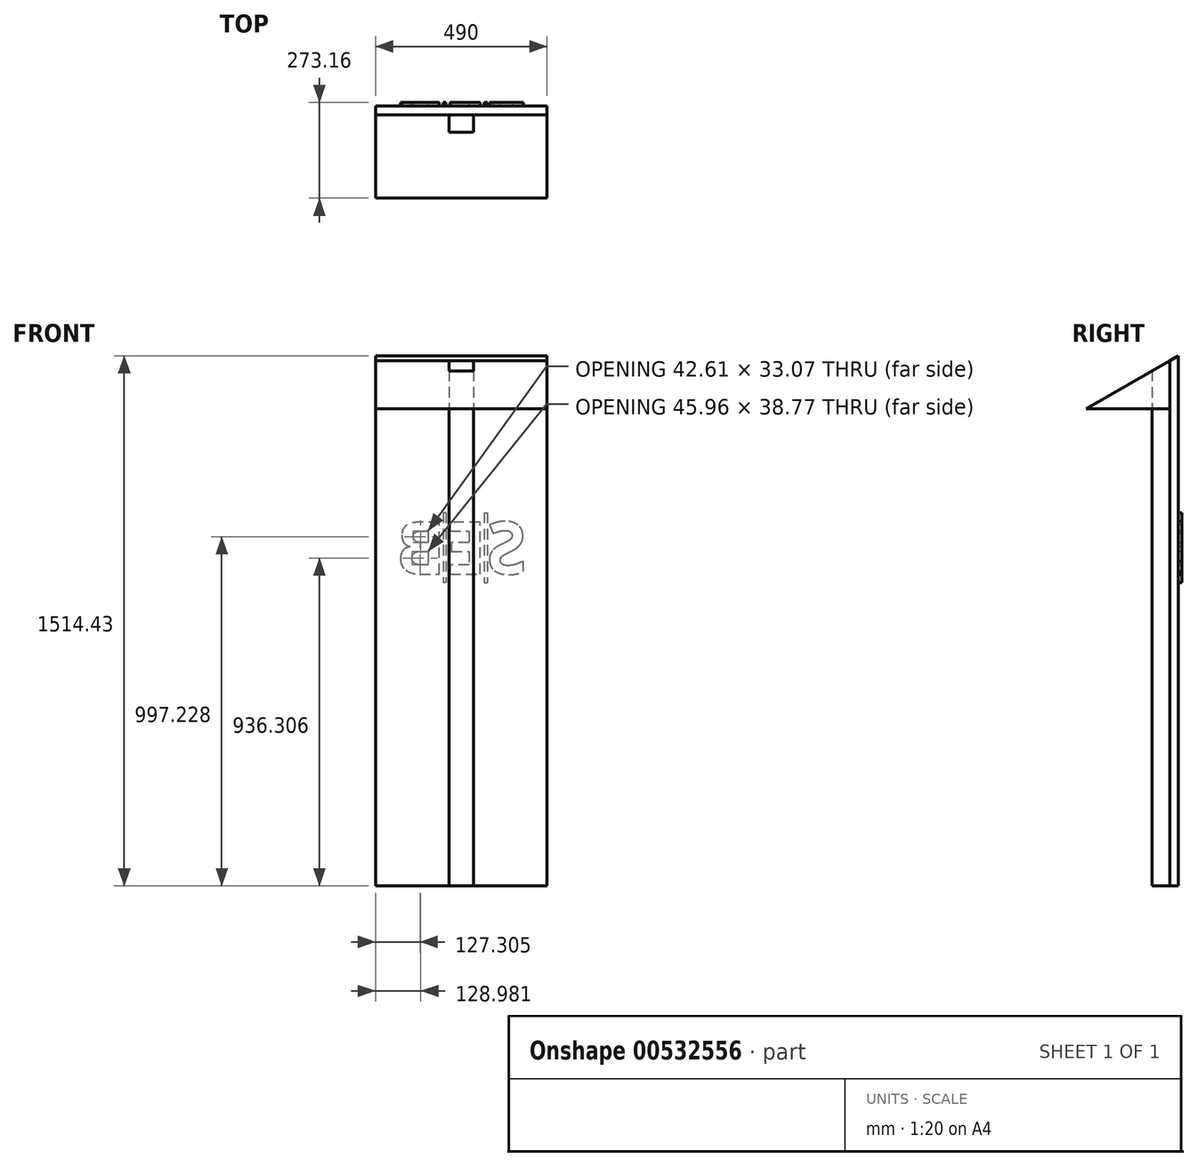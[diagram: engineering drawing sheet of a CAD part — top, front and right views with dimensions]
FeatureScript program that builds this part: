
annotation { "Feature Type Name" : "Feature", "Feature Type Description" : "" }
export const myFeature = defineFeature(function(context is Context, id is Id, definition is map)
    precondition{}
    {
        {
            var Q0;
            Q0=qCreatedBy(makeId("Front.planeOp"),FACE);
            var sketch = newSketch(context, id + "F0", { "sketchPlane" : qUnion([Q0])});
            skLineSegment(sketch, "E0.bottom", {"start": v(-25, 750) * mm, "end": v(25, 750) * mm});
            skLineSegment(sketch, "E0.top", {"start": v(-25, -750) * mm, "end": v(25, -750) * mm});
            skLineSegment(sketch, "E0.left", {"start": v(-25, 750) * mm, "end": v(-25, -750) * mm});
            skLineSegment(sketch, "E0.right", {"start": v(25, 750) * mm, "end": v(25, -750) * mm});
            skPoint(sketch, "E0.middle", {"position": v(0, 0) * mm});
            skSolve(sketch);
        }
        {
            var Q0;
            Q0 = qSketchRegion(id + "F0", true);
            extrude(context, id + "F1", {"entities" : qUnion([Q0]), "depth" : 50 * mm, "offsetDistance" : 25 * mm});
        }
        {
            var Q0;
            Q0=makeQuery(id+"F1.opExtrude","SWEPT_FACE",FACE,{"disambiguationData":[OSD([sQuery(id+"F0.wireOp",EDGE,"E0.left")])]});
            var sketch = newSketch(context, id + "F2", { "sketchPlane" : qUnion([Q0])});
            skLineSegment(sketch, "E1.bottom", {"start": v(0, 750) * mm, "end": v(50, 750) * mm});
            skLineSegment(sketch, "E1.top", {"start": v(0, -750) * mm, "end": v(50, -750) * mm});
            skLineSegment(sketch, "E1.left", {"start": v(0, 750) * mm, "end": v(0, -750) * mm});
            skLineSegment(sketch, "E1.right", {"start": v(50, 750) * mm, "end": v(50, -750) * mm});
            skSolve(sketch);
        }
        {
            var Q0;
            Q0 = qSketchRegion(id + "F2", true);
            extrude(context, id + "F3", {"entities" : qUnion([Q0]), "depth" : 10 * mm, "offsetDistance" : 25 * mm});
        }
        {
            var Q0;
            Q0=makeQuery(id+"F1.opExtrude","SWEPT_FACE",FACE,{"disambiguationData":[OSD([sQuery(id+"F0.wireOp",EDGE,"E0.right")])]});
            var sketch = newSketch(context, id + "F4", { "sketchPlane" : qUnion([Q0])});
            skLineSegment(sketch, "E2.bottom", {"start": v(-50, 750) * mm, "end": v(0, 750) * mm});
            skLineSegment(sketch, "E2.top", {"start": v(-50, -750) * mm, "end": v(0, -750) * mm});
            skLineSegment(sketch, "E2.left", {"start": v(-50, 750) * mm, "end": v(-50, -750) * mm});
            skLineSegment(sketch, "E2.right", {"start": v(0, 750) * mm, "end": v(0, -750) * mm});
            skSolve(sketch);
        }
        {
            var Q0;
            Q0 = qSketchRegion(id + "F4", true);
            extrude(context, id + "F5", {"entities" : qUnion([Q0]), "depth" : 10 * mm, "offsetDistance" : 25 * mm});
        }
        {
            var Q0;
            Q0=makeQuery(id+"F1.opExtrude","CAP_FACE",FACE,{"disambiguationData":[OSD([sQuery(id+"F0.wireOp",EDGE,"E0.bottom"),sQuery(id+"F0.wireOp",EDGE,"E0.top"),sQuery(id+"F0.wireOp",EDGE,"E0.left"),sQuery(id+"F0.wireOp",EDGE,"E0.right")])],"isStart":true});
            var sketch = newSketch(context, id + "F6", { "sketchPlane" : qUnion([Q0])});
            skLineSegment(sketch, "E3.left", {"start": v(-245, 500) * mm, "end": v(-245, -500) * mm});
            skLineSegment(sketch, "E3.right", {"start": v(245, 500) * mm, "end": v(245, -500) * mm});
            skPoint(sketch, "E3.middle", {"position": v(0, 0) * mm});
            skLineSegment(sketch, "E4.top", {"start": v(245, 750) * mm, "end": v(-245, 750) * mm});
            skLineSegment(sketch, "E4.left", {"start": v(245, 500) * mm, "end": v(245, 750) * mm});
            skLineSegment(sketch, "E4.right", {"start": v(-245, 500) * mm, "end": v(-245, 750) * mm});
            skLineSegment(sketch, "E5.top", {"start": v(245, -750) * mm, "end": v(-245, -750) * mm});
            skLineSegment(sketch, "E5.left", {"start": v(245, -500) * mm, "end": v(245, -750) * mm});
            skLineSegment(sketch, "E5.right", {"start": v(-245, -500) * mm, "end": v(-245, -750) * mm});
            skSolve(sketch);
        }
        {
            var Q0;
            Q0 = qSketchRegion(id + "F6", true);
            extrude(context, id + "F7", {"entities" : qUnion([Q0]), "depth" : 25 * mm, "offsetDistance" : 25 * mm});
        }
        {
            var Q0;
            Q0=makeQuery(id+"F5.opExtrude","CAP_FACE",FACE,{"disambiguationData":[OSD([sQuery(id+"F4.wireOp",EDGE,"E2.bottom"),sQuery(id+"F4.wireOp",EDGE,"E2.top"),sQuery(id+"F4.wireOp",EDGE,"E2.left"),sQuery(id+"F4.wireOp",EDGE,"E2.right")])],"isStart":false});
            var sketch = newSketch(context, id + "F8", { "sketchPlane" : qUnion([Q0])});
            skLineSegment(sketch, "E6", {"start": v(0, 750) * mm, "end": v(-50, 750) * mm});
            skLineSegment(sketch, "E7", {"start": v(0, 750) * mm, "end": v(-50, 721.13) * mm});
            skLineSegment(sketch, "E8", {"start": v(-50, 721.13) * mm, "end": v(-50, 750) * mm});
            skSolve(sketch);
        }
        {
            var Q0;
            Q0 = qSketchRegion(id + "F8", true);
            extrude(context, id + "F9", {"entities" : qUnion([Q0]), "operationType" : NewBodyOperationType.REMOVE, "oppositeDirection" : true, "depth" : 100 * mm, "offsetDistance" : 25 * mm});
        }
        {
            var Q0;
            Q0=makeQuery(id+"F7.opExtrude","SWEPT_FACE",FACE,{"disambiguationData":[OSD([sQuery(id+"F6.wireOp",EDGE,"E3.left"),sQuery(id+"F6.wireOp",EDGE,"E4.right")])]});
            var sketch = newSketch(context, id + "F10", { "sketchPlane" : qUnion([Q0])});
            skLineSegment(sketch, "E9", {"start": v(0, 750) * mm, "end": v(25, 764.43) * mm});
            skLineSegment(sketch, "E10", {"start": v(25, 764.43) * mm, "end": v(25, 750) * mm});
            skLineSegment(sketch, "E11", {"start": v(25, 750) * mm, "end": v(0, 750) * mm});
            skSolve(sketch);
        }
        {
            var Q0;
            Q0 = qSketchRegion(id + "F10", true);
            extrude(context, id + "F11", {"entities" : qUnion([Q0]), "operationType" : NewBodyOperationType.ADD, "oppositeDirection" : true, "depth" : 490 * mm, "offsetDistance" : 25 * mm});
        }
        {
            var Q0;
            Q0=makeQuery(id+"F11.boolean.opBoolean","MERGE",FACE,{"derivedFrom":[makeQuery(id+"F7.opExtrude","CAP_FACE",FACE,{"disambiguationData":[OSD([sQuery(id+"F6.wireOp",EDGE,"E3.top"),sQuery(id+"F6.wireOp",EDGE,"E3.left"),sQuery(id+"F6.wireOp",EDGE,"E3.right"),sQuery(id+"F6.wireOp",EDGE,"E4.top"),sQuery(id+"F6.wireOp",EDGE,"E4.left"),sQuery(id+"F6.wireOp",EDGE,"E4.right")])],"isStart":false}),makeQuery(id+"F11.opExtrude","SWEPT_FACE",FACE,{"disambiguationData":[OSD([sQuery(id+"F10.wireOp",EDGE,"E10")])]})]});
            var sketch = newSketch(context, id + "F12", { "sketchPlane" : qUnion([Q0])});
            skText(sketch, "E12", { "text": "SEB", "fontName": "OpenSans-Bold.ttf"});
            skLineSegment(sketch, "E13.bottom", {"start": v(-65.83, 315.88) * mm, "end": v(-73.83, 315.88) * mm});
            skLineSegment(sketch, "E13.top", {"start": v(-65.83, 115.88) * mm, "end": v(-73.83, 115.88) * mm});
            skLineSegment(sketch, "E13.left", {"start": v(-65.83, 315.88) * mm, "end": v(-65.83, 115.88) * mm});
            skLineSegment(sketch, "E13.right", {"start": v(-73.83, 315.88) * mm, "end": v(-73.83, 115.88) * mm});
            skPoint(sketch, "E13.middle", {"position": v(-69.83, 215.88) * mm});
            skPoint(sketch, "E13.middle.positionSnap0", {"position": v(-186.96, 215.88) * mm});
            skPoint(sketch, "E13.centerSnap0", {"position": v(-186.96, 215.88) * mm});
            skLineSegment(sketch, "E14.bottom", {"start": v(43.62, 315.88) * mm, "end": v(51.62, 315.88) * mm});
            skLineSegment(sketch, "E14.top", {"start": v(43.62, 115.88) * mm, "end": v(51.62, 115.88) * mm});
            skLineSegment(sketch, "E14.left", {"start": v(43.62, 315.88) * mm, "end": v(43.62, 115.88) * mm});
            skLineSegment(sketch, "E14.right", {"start": v(51.62, 315.88) * mm, "end": v(51.62, 115.88) * mm});
            skPoint(sketch, "E14.middle", {"position": v(47.62, 215.88) * mm});
            skPoint(sketch, "E14.middle.positionSnap0", {"position": v(0, 215.88) * mm});
            skPoint(sketch, "E14.centerSnap0", {"position": v(0, 215.88) * mm});
            const initialGuessF12  = {"E12": [-0.18696, 0.14088, 1, 0, 0.15]};
            skSetInitialGuess(sketch, initialGuessF12);
            skSolve(sketch);
        }
        {
            var Q0;
            Q0 = qSketchRegion(id + "F12", true);
            extrude(context, id + "F13", {"entities" : qUnion([Q0]), "depth" : 10 * mm, "offsetDistance" : 25 * mm});
        }
        {
            var Q0;
            Q0=makeQuery(id+"F11.boolean.opBoolean","MERGE",FACE,{"derivedFrom":[makeQuery(id+"F7.opExtrude","SWEPT_FACE",FACE,{"disambiguationData":[OSD([sQuery(id+"F6.wireOp",EDGE,"E3.left"),sQuery(id+"F6.wireOp",EDGE,"E4.right"),sQuery(id+"F6.wireOp",EDGE,"E5.right")])]}),makeQuery(id+"F11.opExtrude","CAP_FACE",FACE,{"disambiguationData":[OSD([sQuery(id+"F10.wireOp",EDGE,"E9"),sQuery(id+"F10.wireOp",EDGE,"E10"),sQuery(id+"F10.wireOp",EDGE,"E11")])],"isStart":true})]});
            var sketch = newSketch(context, id + "F14", { "sketchPlane" : qUnion([Q0])});
            skLineSegment(sketch, "E15", {"start": v(0, 750) * mm, "end": v(-238.16, 612.5) * mm});
            skLineSegment(sketch, "E16", {"start": v(-238.16, 612.5) * mm, "end": v(0, 612.5) * mm});
            skLineSegment(sketch, "E17", {"start": v(0, 612.5) * mm, "end": v(0, 750) * mm});
            skSolve(sketch);
        }
        {
            var Q0;
            Q0 = qSketchRegion(id + "F14", true);
            extrude(context, id + "F15", {"entities" : qUnion([Q0]), "oppositeDirection" : true, "depth" : 490 * mm, "offsetDistance" : 25 * mm});
        }
    });
